# Revit family: PRD_AR_ShwrThrmsttcVlvs_ThermostatBathMixer_F4MT2001
name_source: partatom
category: Plumbing Fixtures
units: mm (PartAtom-declared; Revit-internal decimal feet)

## family parameters
Cut with Voids When Loaded = Yes
Host = Face
OmniClass Number = 23.45.55.17
OmniClass Title = Mixing Faucets
Part Type = Normal
Room Calculation Point = No
Round Connector Dimension = Use Diameter
Shared = No

## types (1)
- F4MT2001
    AdjustableFlowTime = no
    AssetType = Fixed
    BIMObjectName = PRD_AR_ShowerThermostaticValves_ThermostatBathMixer_F4MT2001
    BodyMaterial = PRD_AR_ChromatedBrass_HighPolished
    Category = Pr_40_20_87_80, Shower thermostatic valves
    Circulation = no
    CloseOffRating = 0.0 Pa
    Color = chrome-look (glossy)
    CompatibleA3000Open = no
    ConnectionWithPayWaterDispenser = not possible
    Default Elevation = 1219 mm
    Description = F4MT-Med thermostat bath mixer with fixed spout as a two-handle wall-mounted mixer DN 15, fitting group I, for wall mounting for baths in the healthcare and nursing sector, for connecting to hot and cold water. Ceramic valve cartridge with rotary handle for flow regulation, mixer water shut-off, as well as integrated diverter for bathtub and hand shower. Thermostat-controlled mixer cartridge with expansion element and active scald protection, fail-safe against backflow as well as adjustable, turn-proof temperature stop, preset to 38 °C and option to carry out manual thermal disinfection. Tap optimised for cleaning with ergonomically designed handles, scald-protected safe-touch housing with hand shower connection 13 l/min, G 1/2 B, bath spout with laminar jet controller 20 l/min and backflow preventer. All-metal construction, high-polished chrome-plated. Double-walled tap housing for reducing the heat transfer from the tap housing to the cold water line, with volume-reduced and smooth water lines. With adjustable connections with strainers, fully covered by depth-adjustable screw rosettes. 180 mm bath spout projection.
    DiameterNominal = 15  [stored 0.0492126 ft]
    DurationUnit = year
    Features = For connection to hot water and cold water. 180 mm bath spout projection.
    Finish = polished chrome-plated
    FlowCoefficient = 0
    ForHandShower = yes
    FunctionalPrinciple = manual
    HygieneFlushing = no
    IfcExportAs = IfcValveType
    IfcExportType = MIXING
    InletSize = DN 15
    LockingMechanism = Top section, ceramic
    Manufacturer = KWC Group AG
    ManufacturerName = KWC Group AG
    ManufacturerURL = www.kwc.com
    Material = Brass
    MixerControl = OTHER
    Model = F4MT2001
    ModelNumber = 3600000189
    ModelReference = F4MT2001
    NBSDescription = Shower mixers
    NBSReference = 45-35-70/335
    Name = F4MT-Med thermostat bath mixer F4MT2001
    NominalDepth = 0 mm  [stored 0 ft]
    NominalHeight = 0 mm  [stored 0 ft]
    NominalWidth = 300 mm
    OutletConnectionSize = 15 mm  [stored 0.0492126 ft]
    PositionOfWaterConnection = from backside
    ProductInformation = http://pim.kwc.com
    ShowerPipeDraining = no
    Size = 15
    Status = New
    SurfaceFinishCasing = chromed
    SurfaceFinishFitting = chromed
    SurfaceTreatmentFitting = polished
    TailorMade = no
    TemperatureLimit = yes
    TestPressure = 0.0 Pa
    ThermalDisinfection = manual thermal disinfection
    TypeOfMixing = with thermostat
    TypeOfMounting = wall mounting
    TypeOfOperation = manual operation
    TypeOfShower = wall fitting
    URL = www.kwc.com
    Uniclass2015Code = Pr_40_20_87_80
    Uniclass2015Title = Shower thermostatic valves
    Uniclass2015Version = Products v1.32
    ValveMechanism = OTHER
    ValveOperation = LEVER
    ValvePattern = ANGLED_2_PORT
    Version = 1
    WarrantyDurationUnit = year
    WaterConnection = S-unions
    WithShowerSet = no
    WithSoapDish = no
    WorkingPressure = 0.0 Pa

note: [stored X ft] marks values corroborated as IEEE doubles in the binary element streams (Revit-internal decimal feet)

## geometry (parser evidence)
native form markers: Sweep x5
no freeform markers — native parametric forms only
